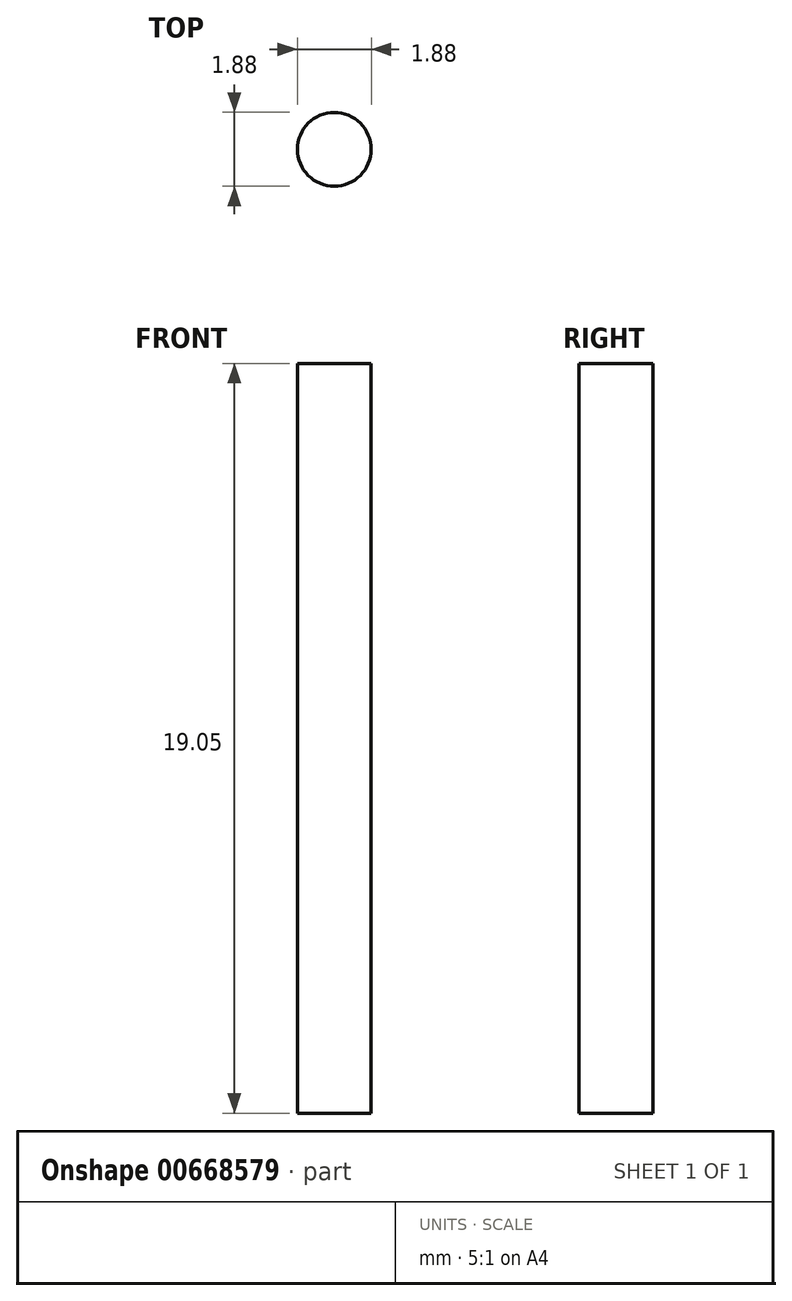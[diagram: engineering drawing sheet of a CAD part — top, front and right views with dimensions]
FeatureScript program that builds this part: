
annotation { "Feature Type Name" : "Feature", "Feature Type Description" : "" }
export const myFeature = defineFeature(function(context is Context, id is Id, definition is map)
    precondition{}
    {
        {
            var Q0;
            Q0=qCreatedBy(makeId("Top.planeOp"),FACE);
            var sketch = newSketch(context, id + "F0", { "sketchPlane" : qUnion([Q0])});
            skCircle(sketch, "E0", {"center": v(0, 0) * mm, "radius": 0.94 * mm});
            skSolve(sketch);
        }
        {
            var Q0;
            Q0=makeQuery(id+"F0.imprint","IMPRINT",FACE,{"disambiguationData":[TD([[makeQuery(id+"F0.imprint","IMPRINT",EDGE,{"derivedFrom":sQuery(id+"F0.wireOp",EDGE,"E0")}),1.0]])]});
            extrude(context, id + "F1", {"entities" : qUnion([Q0]), "depth" : 19.05 * mm, "offsetDistance" : 25.4 * mm});
        }
    });
